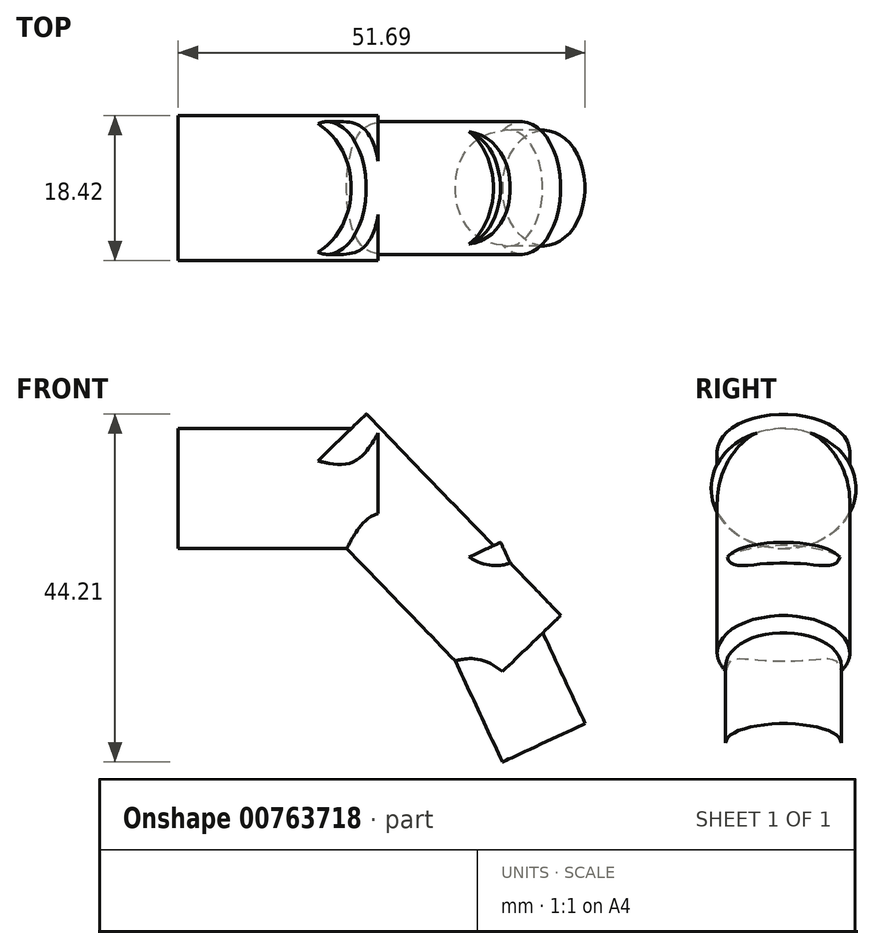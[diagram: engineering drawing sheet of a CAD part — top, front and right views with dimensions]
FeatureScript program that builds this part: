
annotation { "Feature Type Name" : "Feature", "Feature Type Description" : "" }
export const myFeature = defineFeature(function(context is Context, id is Id, definition is map)
    precondition{}
    {
        {
            var Q0;
            Q0=qCreatedBy(makeId("Right.planeOp"),FACE);
            var sketch = newSketch(context, id + "F0", { "sketchPlane" : qUnion([Q0])});
            skEllipse(sketch, "E0", {"center": v(0, 0) * mm, "majorRadius": 9.2 * mm, "minorRadius": 7.62 * mm, "majorAxis": v(1, 0)});
            skSolve(sketch);
        }
        {
            var Q0;
            Q0=qCreatedBy(makeId("Front.planeOp"),FACE);
            var sketch = newSketch(context, id + "F1", { "sketchPlane" : qUnion([Q0])});
            skLineSegment(sketch, "E1", {"start": v(0, 0) * mm, "end": v(23.55, 0) * mm});
            skLineSegment(sketch, "E2", {"start": v(23.55, 0) * mm, "end": v(39.13, -16.13) * mm});
            skLineSegment(sketch, "E3", {"start": v(39.13, -16.13) * mm, "end": v(43.42, -25.34) * mm});
            skPoint(sketch, "E4", {"position": v(31.34, -8.07) * mm});
            skPoint(sketch, "E5", {"position": v(11.77, 0) * mm});
            skPoint(sketch, "E6", {"position": v(41.27, -20.74) * mm});
            skPoint(sketch, "E7", {"position": v(41.44, -20.62) * mm});
            skSolve(sketch);
        }
        {
            var Q0;
            Q0=sQuery(id+"F1.wireOp",VERTEX,"E4");
            var Q1;
            Q1=sQuery(id+"F1.wireOp",EDGE,"E2");
            cPlane(context, id + "F2", {"entities" : qUnion([Q0, Q1]), "cplaneType" : CPlaneType.LINE_POINT, "offset" : 25.4 * mm, "width" : 152.4 * mm, "height" : 152.4 * mm});
        }
        {
            var Q0;
            Q0=qCreatedBy(id+"F2.planeOp",FACE);
            var sketch = newSketch(context, id + "F3", { "sketchPlane" : qUnion([Q0])});
            skEllipse(sketch, "E8", {"center": v(16.94, 0) * mm, "majorRadius": 8.43 * mm, "minorRadius": 6.83 * mm, "majorAxis": v(0, -1)});
            skSolve(sketch);
        }
        {
            var Q0;
            Q0=sQuery(id+"F1.wireOp",EDGE,"E3");
            var Q1;
            Q1=sQuery(id+"F1.wireOp",VERTEX,"E7");
            cPlane(context, id + "F4", {"entities" : qUnion([Q0, Q1]), "cplaneType" : CPlaneType.LINE_POINT, "offset" : 25.4 * mm, "width" : 152.4 * mm, "height" : 152.4 * mm});
        }
        {
            var Q0;
            Q0=qCreatedBy(id+"F4.planeOp",FACE);
            var sketch = newSketch(context, id + "F5", { "sketchPlane" : qUnion([Q0])});
            skEllipse(sketch, "E9", {"center": v(28.44, 0) * mm, "majorRadius": 7.37 * mm, "minorRadius": 5.8 * mm, "majorAxis": v(0, -1)});
            skSolve(sketch);
        }
        {
            var Q0;
            Q0 = qSketchRegion(id + "F0", true);
            extrude(context, id + "F6", {"entities" : qUnion([Q0]), "depth" : 25.4 * mm, "offsetDistance" : 25.4 * mm});
        }
        {
            var Q0;
            Q0 = qSketchRegion(id + "F3", true);
            extrude(context, id + "F7", {"entities" : qUnion([Q0]), "operationType" : NewBodyOperationType.ADD, "endBound" : BoundingType.SYMMETRIC, "depth" : 35.56 * mm, "offsetDistance" : 25.4 * mm});
        }
        {
            var Q0;
            Q0 = qSketchRegion(id + "F5", true);
            extrude(context, id + "F8", {"entities" : qUnion([Q0]), "operationType" : NewBodyOperationType.ADD, "endBound" : BoundingType.SYMMETRIC, "depth" : 25.4 * mm, "offsetDistance" : 25.4 * mm});
        }
    });
